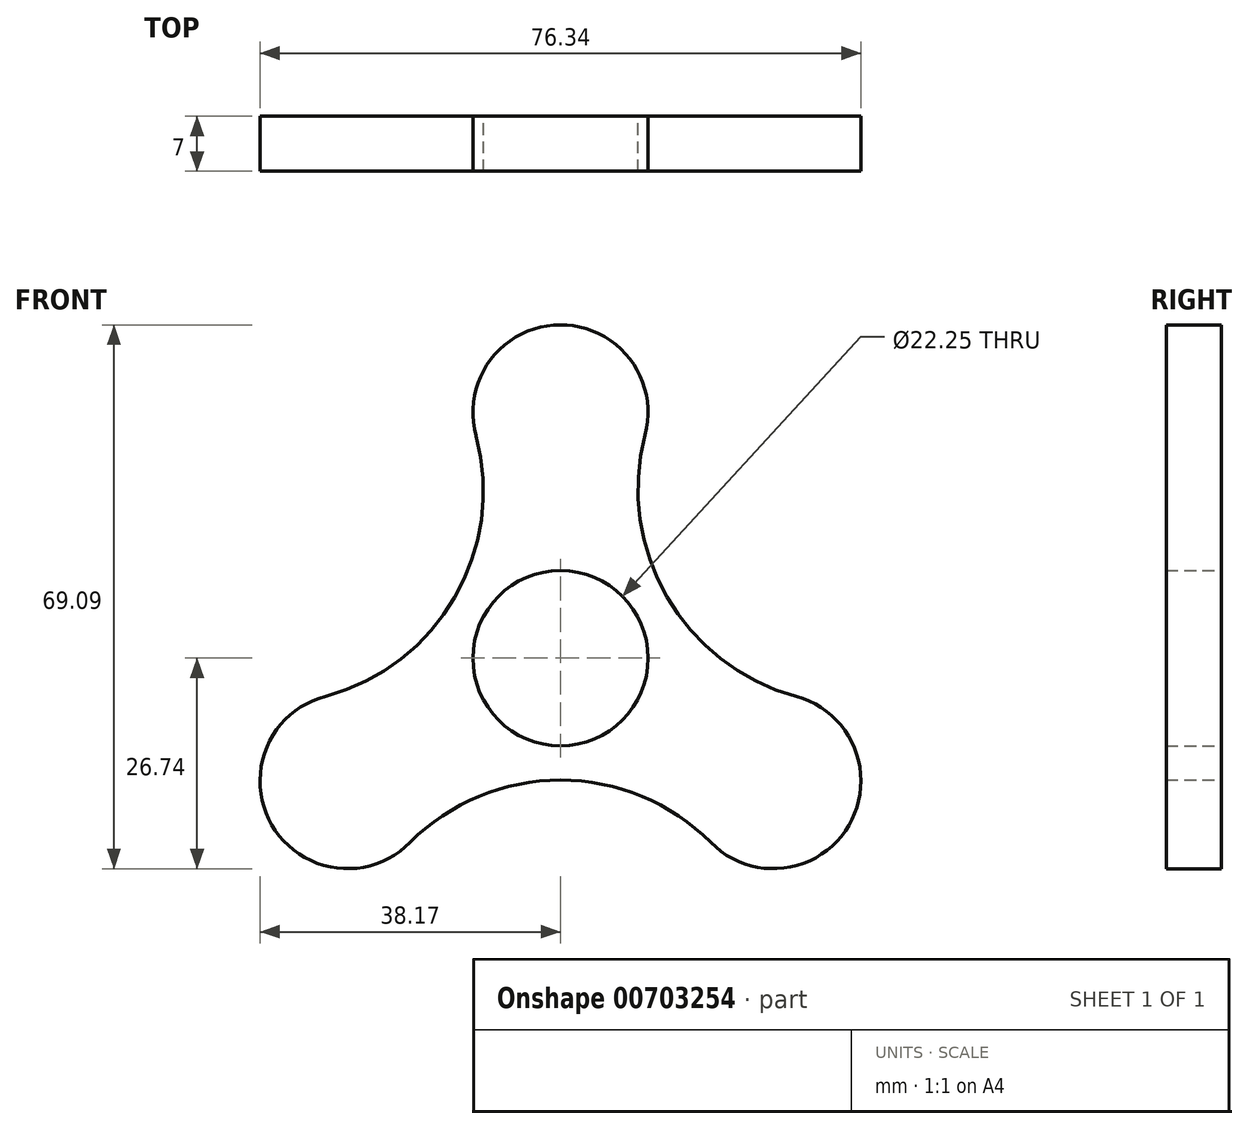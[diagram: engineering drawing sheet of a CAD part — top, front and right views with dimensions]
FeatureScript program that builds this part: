
annotation { "Feature Type Name" : "Feature", "Feature Type Description" : "" }
export const myFeature = defineFeature(function(context is Context, id is Id, definition is map)
    precondition{}
    {
        {
            var Q0;
            Q0=qCreatedBy(makeId("Front.planeOp"),FACE);
            var sketch = newSketch(context, id + "F0", { "sketchPlane" : qUnion([Q0])});
            skCircle(sketch, "E0", {"center": v(0, 0) * mm, "radius": 11.12 * mm});
            skArc(sketch, "E1", {"start": v(10.76, 28.38) * mm, "mid": v(-0.06, 42.35) * mm, "end": v(-10.73, 28.27) * mm});
            skArc(sketch, "E2.1.0", {"start": v(-29.83, -4.84) * mm, "mid": v(-36.67, -21.19) * mm, "end": v(-19.1, -23.4) * mm});
            skArc(sketch, "E2.2.0", {"start": v(19.1, -23.4) * mm, "mid": v(36.64, -21.24) * mm, "end": v(29.96, -4.88) * mm});
            skArc(sketch, "E3", {"start": v(-29.96, -4.88) * mm, "mid": v(-13.46, 7.68) * mm, "end": v(-10.72, 28.24) * mm});
            skArc(sketch, "E4", {"start": v(10.76, 28.38) * mm, "mid": v(13.52, 7.8) * mm, "end": v(29.96, -4.88) * mm});
            skArc(sketch, "E5", {"start": v(19.2, -23.5) * mm, "mid": v(0, -15.48) * mm, "end": v(-19.2, -23.5) * mm});
            skArc(sketch, "E6.filletArc", {"start": v(-10.72, 28.24) * mm, "mid": v(-10.72, 28.26) * mm, "end": v(-10.73, 28.27) * mm});
            skSolve(sketch);
        }
        {
            var Q0;
            Q0 = qSketchRegion(id + "F0", true);
            extrude(context, id + "F1", {"entities" : qUnion([Q0]), "depth" : 7 * mm, "offsetDistance" : 25 * mm});
        }
    });
